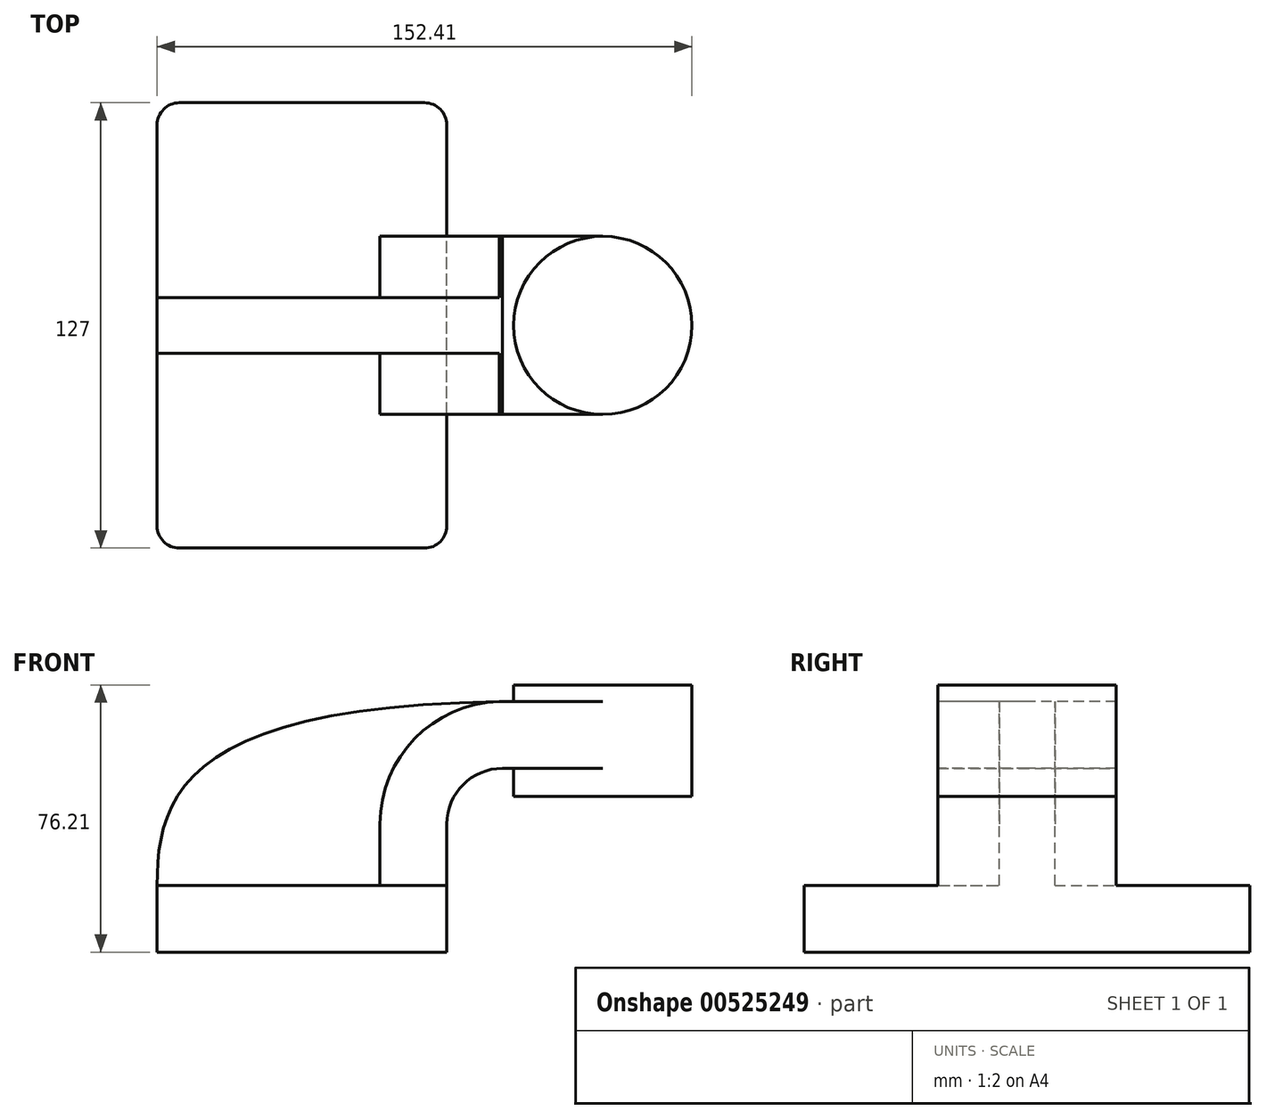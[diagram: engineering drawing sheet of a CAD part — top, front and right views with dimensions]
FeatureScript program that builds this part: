
annotation { "Feature Type Name" : "Feature", "Feature Type Description" : "" }
export const myFeature = defineFeature(function(context is Context, id is Id, definition is map)
    precondition{}
    {
        {
            var Q0;
            Q0=qCreatedBy(makeId("Front.planeOp"),FACE);
            var sketch = newSketch(context, id + "F0", { "sketchPlane" : qUnion([Q0])});
            skLineSegment(sketch, "E0.bottom", {"start": v(41.28, -9.52) * mm, "end": v(-41.28, -9.53) * mm});
            skLineSegment(sketch, "E0.top", {"start": v(41.28, 9.53) * mm, "end": v(-41.28, 9.53) * mm});
            skLineSegment(sketch, "E0.left", {"start": v(41.28, -9.52) * mm, "end": v(41.28, 9.53) * mm});
            skLineSegment(sketch, "E0.right", {"start": v(-41.28, -9.52) * mm, "end": v(-41.28, 9.53) * mm});
            skPoint(sketch, "E0.middle", {"position": v(0, 0) * mm});
            skLineSegment(sketch, "E1.bottom", {"start": v(111.12, 34.93) * mm, "end": v(60.33, 34.93) * mm});
            skLineSegment(sketch, "E1.top", {"start": v(111.12, 66.68) * mm, "end": v(60.32, 66.68) * mm});
            skLineSegment(sketch, "E1.left", {"start": v(111.12, 34.93) * mm, "end": v(111.12, 66.68) * mm});
            skLineSegment(sketch, "E1.right", {"start": v(60.33, 34.93) * mm, "end": v(60.32, 66.68) * mm});
            skPoint(sketch, "E1.middle", {"position": v(85.72, 50.8) * mm});
            skLineSegment(sketch, "E2", {"start": v(41.28, 9.53) * mm, "end": v(41.28, 27) * mm});
            skArc(sketch, "E3", {"start": v(41.27, 27) * mm, "mid": v(45.92, 38.23) * mm, "end": v(57.15, 42.88) * mm});
            skLineSegment(sketch, "E4", {"start": v(57.15, 42.88) * mm, "end": v(85.73, 42.88) * mm});
            skLineSegment(sketch, "E5.0", {"start": v(57.15, 61.93) * mm, "end": v(85.73, 61.93) * mm});
            skArc(sketch, "E5.1", {"start": v(22.23, 27) * mm, "mid": v(32.45, 51.7) * mm, "end": v(57.15, 61.93) * mm});
            skLineSegment(sketch, "E5.2", {"start": v(22.23, 9.53) * mm, "end": v(22.23, 27) * mm});
            skLineSegment(sketch, "E6", {"start": v(85.72, 34.93) * mm, "end": v(85.72, 66.68) * mm});
            skFitSpline(sketch, "E7", {"points": [v(-41.28, 9.53) * mm, v(57.15, 61.93) * mm], "startDerivative": vector(-0.14, 75.7) * mm, "endDerivative": vector(272.9, 3.45) * mm});
            skSolve(sketch);
        }
        {
            var Q0;
            Q0=makeQuery(id+"F0.imprint","IMPRINT",FACE,{"disambiguationData":[TD([[makeQuery(id+"F0.imprint","IMPRINT",EDGE,{"derivedFrom":sQuery(id+"F0.wireOp",EDGE,"E0.bottom")}),-1.0]])]});
            extrude(context, id + "F1", {"entities" : qUnion([Q0]), "endBound" : BoundingType.SYMMETRIC, "depth" : 127 * mm, "offsetDistance" : 25.4 * mm});
        }
        {
            var Q0;
            {var subQ1=sQuery(id+"F0.wireOp",EDGE,"E2");Q0=makeQuery(id+"F0.imprint","IMPRINT",FACE,{"disambiguationData":[TD([[makeQuery(id+"F0.imprint","IMPRINT",EDGE,{"derivedFrom":subQ1}),1.0]])]});}
            var Q1;
            {var subQ0=sQuery(id+"F0.wireOp",EDGE,"E4");var subQ1=sQuery(id+"F0.wireOp",EDGE,"E1.right");var subQ2=makeQuery(id+"F0.imprint","INTERSECT",VERTEX,{"derivedFrom":[subQ1,subQ0]});Q1=makeQuery(id+"F0.imprint","IMPRINT",FACE,{"disambiguationData":[TD([[makeQuery(id+"F0.imprint","IMPRINT",EDGE,{"disambiguationData":[TD([[subQ2,-1.0]])],"derivedFrom":subQ1}),-1.0]])]});}
            extrude(context, id + "F2", {"entities" : qUnion([Q0, Q1]), "operationType" : NewBodyOperationType.ADD, "endBound" : BoundingType.SYMMETRIC, "depth" : 50.8 * mm, "offsetDistance" : 25.4 * mm});
        }
        {
            var Q0;
            {var subQ3=sQuery(id+"F0.wireOp",EDGE,"E5.2");Q0=makeQuery(id+"F0.imprint","IMPRINT",FACE,{"disambiguationData":[TD([[makeQuery(id+"F0.imprint","IMPRINT",EDGE,{"derivedFrom":subQ3}),1.0]])]});}
            extrude(context, id + "F3", {"entities" : qUnion([Q0]), "operationType" : NewBodyOperationType.ADD, "endBound" : BoundingType.SYMMETRIC, "depth" : 15.88 * mm, "offsetDistance" : 25.4 * mm});
        }
        {
            var Q0;
            {var subQ0=sQuery(id+"F0.wireOp",EDGE,"E1.left");Q0=makeQuery(id+"F0.imprint","IMPRINT",FACE,{"disambiguationData":[TD([[makeQuery(id+"F0.imprint","IMPRINT",EDGE,{"derivedFrom":subQ0}),1.0]])]});}
            var Q1;
            Q1=sQuery(id+"F0.wireOp",EDGE,"E6");
            revolve(context, id + "F4", {"operationType" : NewBodyOperationType.ADD, "entities" : qUnion([Q0]), "axis" : qUnion([Q1]), "revolveType" : RevolveType.FULL});
        }
        {
            var Q0;
            Q0=makeQuery(id+"F1.opExtrude","CAP_EDGE",EDGE,{"disambiguationData":[OSD([sQuery(id+"F0.wireOp",EDGE,"E0.left")])],"isStart":false});
            var Q1;
            Q1=makeQuery(id+"F1.opExtrude","CAP_EDGE",EDGE,{"disambiguationData":[OSD([sQuery(id+"F0.wireOp",EDGE,"E0.left")])],"isStart":true});
            var Q2;
            Q2=makeQuery(id+"F1.opExtrude","CAP_EDGE",EDGE,{"disambiguationData":[OSD([sQuery(id+"F0.wireOp",EDGE,"E0.right")])],"isStart":false});
            var Q3;
            Q3=makeQuery(id+"F1.opExtrude","CAP_EDGE",EDGE,{"disambiguationData":[OSD([sQuery(id+"F0.wireOp",EDGE,"E0.right")])],"isStart":true});
            fillet(context, id + "F5", {"entities" : qUnion([Q0, Q1, Q2, Q3]), "radius" : 6.35 * mm, "tangentPropagation" : true, "allowEdgeOverflow" : false});
        }
    });
